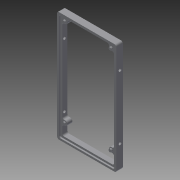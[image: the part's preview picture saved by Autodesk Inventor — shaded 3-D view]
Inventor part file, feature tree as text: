
AUTODESK INVENTOR PART (.ipt)
format: ipt  version: 2015 (Build 190159000, 159)  size: 210,944 bytes
history: native  units: mm
features: extrude x4, sketch x3
ambient origin geometry x8: Origin, YZ Plane, XZ Plane, XY Plane, X Axis, Y Axis, Z Axis, Center Point
bodies: Solid1 (feature_tree)
feature tree (7):
  extrude  "Extrusion1"  Depth=7.0mm TaperAngle=0.0deg
  extrude  "Extrusion2"  Depth=59.15mm
  extrude  "Extrusion5"  Depth=1.6mm TaperAngle=0.0deg
  extrude  "Extrusion6"  Depth=4.0mm
  sketch  "Sketch2"  dims[d0=4.0mm d2=4.0mm d8=7.0mm d9=0.0mm]
  sketch  "Sketch5"  dims[d10=4.0mm d26=59.15mm]
  sketch  "Sketch6"  dims[d27=113.76mm d28=1.6mm d29=0.0mm d43=4.0mm d51=8.852mm d54=4.0mm d67=8.0mm d77=57.15mm d78=3.81mm d79=3.81mm d80=3.81mm d81=3.81mm d82=3.0mm d85=111.76mm d88=3.81mm d99=1.0mm d100=1.0mm d101=3.0mm d103=1.0mm d104=1.0mm d107=3.0mm d109=3.0mm d111=5.0mm d115=1.0mm d116=5.0mm d121=1.0mm d122=3.0mm d123=2.0mm d129=1.0mm d131=2.0mm d132=2.0mm d133=3.0mm d134=3.0mm d135=3.0mm d136=3.0mm d137=25.0mm d138=25.0mm d139=70.0mm d140=0.0mm d141=3.0mm d142=1.5mm d143=5.0mm d144=1.0mm d145=2.0mm d146=1.6mm d147=5.4mm d148=0.0mm d149=0.0mm d150=2.5mm d151=3.0mm d152=3.0mm d154=5.0mm d155=2.0mm d156=1.0mm d157=12.97mm]
